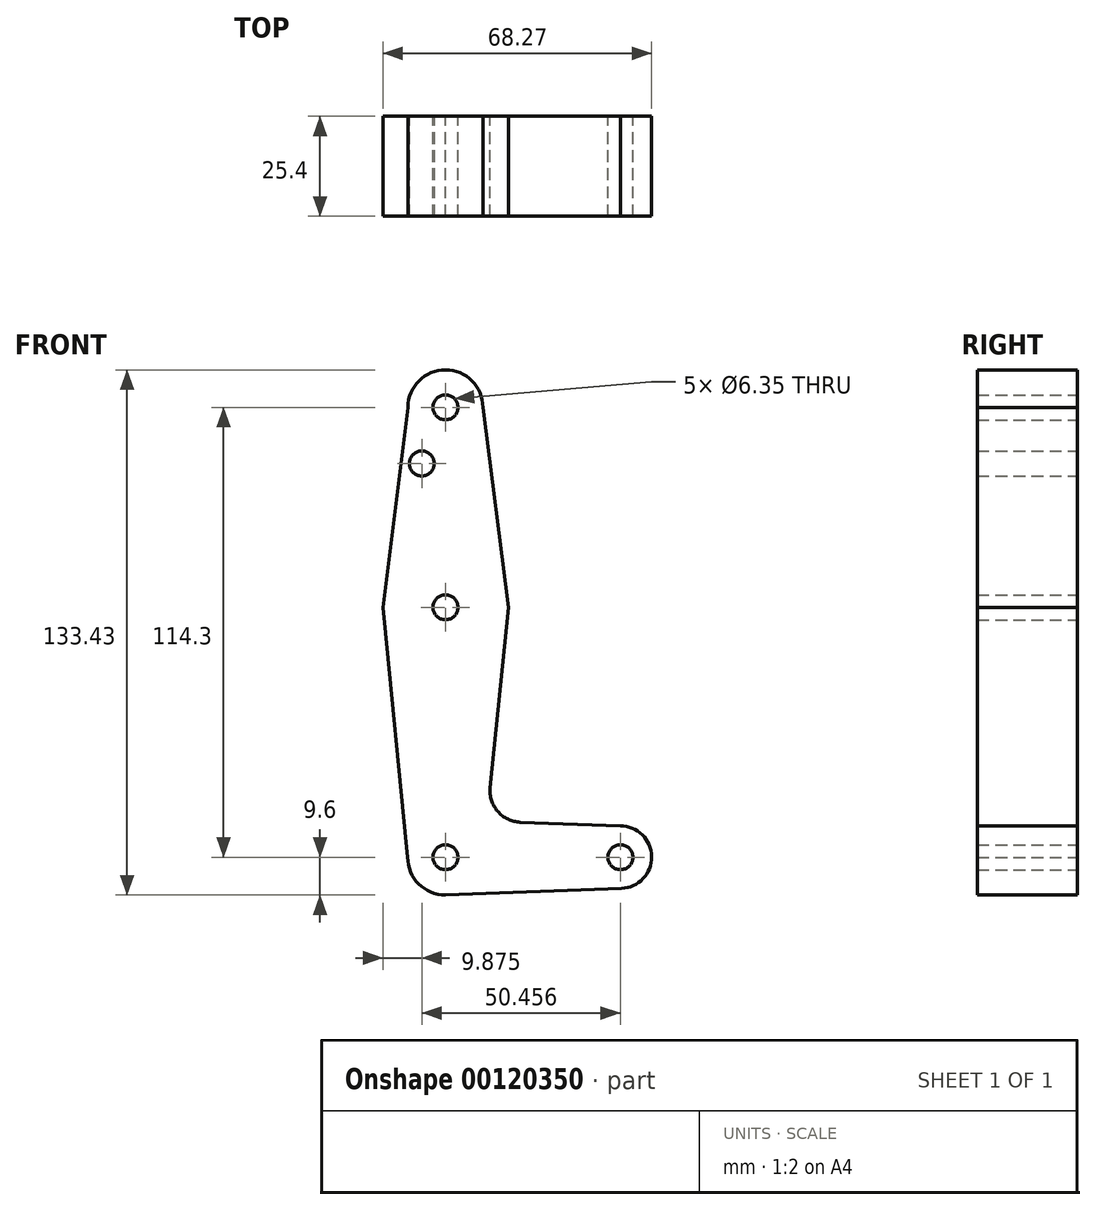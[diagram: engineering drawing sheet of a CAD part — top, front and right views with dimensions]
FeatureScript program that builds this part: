
annotation { "Feature Type Name" : "Feature", "Feature Type Description" : "" }
export const myFeature = defineFeature(function(context is Context, id is Id, definition is map)
    precondition{}
    {
        {
            var Q0;
            Q0=qCreatedBy(makeId("Front.planeOp"),FACE);
            var sketch = newSketch(context, id + "F0", { "sketchPlane" : qUnion([Q0])});
            skLineSegment(sketch, "E0", {"start": v(0, 0) * mm, "end": v(0, 114.3) * mm, "construction": true});
            skLineSegment(sketch, "E1", {"start": v(0, 0) * mm, "end": v(44.45, 0) * mm, "construction": true});
            skCircle(sketch, "E2", {"center": v(0, 0) * mm, "radius": 9.6 * mm});
            skCircle(sketch, "E3", {"center": v(0, 63.5) * mm, "radius": 15.88 * mm});
            skCircle(sketch, "E4", {"center": v(0, 114.3) * mm, "radius": 9.53 * mm});
            skCircle(sketch, "E5", {"center": v(44.45, 0) * mm, "radius": 7.94 * mm});
            skLineSegment(sketch, "E6", {"start": v(-9.52, 114.3) * mm, "end": v(-15.88, 63.5) * mm});
            skLineSegment(sketch, "E7", {"start": v(9.52, 114.3) * mm, "end": v(16, 63.5) * mm});
            skLineSegment(sketch, "E8", {"start": v(44.45, 7.94) * mm, "end": v(19, 8.9) * mm});
            skLineSegment(sketch, "E9", {"start": v(0, -9.6) * mm, "end": v(44.75, -7.93) * mm});
            skLineSegment(sketch, "E10", {"start": v(-9.6, 0) * mm, "end": v(-15.88, 63.5) * mm});
            skLineSegment(sketch, "E11", {"start": v(11.38, 17.64) * mm, "end": v(16, 63.5) * mm});
            skCircle(sketch, "E12", {"center": v(0, 114.3) * mm, "radius": 3.18 * mm});
            skCircle(sketch, "E13", {"center": v(0, 63.5) * mm, "radius": 3.17 * mm});
            skCircle(sketch, "E14", {"center": v(0, 0) * mm, "radius": 3.18 * mm});
            skCircle(sketch, "E15", {"center": v(44.45, 0) * mm, "radius": 3.18 * mm});
            skCircle(sketch, "E16", {"center": v(-6, 100.03) * mm, "radius": 3.18 * mm});
            skArc(sketch, "E17.filletArc", {"start": v(11.38, 17.64) * mm, "mid": v(13.3, 11.62) * mm, "end": v(19, 8.9) * mm});
            skSolve(sketch);
        }
        {
            var Q0;
            {var subQ8=sQuery(id+"F0.wireOp",EDGE,"E8");Q0=makeQuery(id+"F0.imprint","IMPRINT",FACE,{"disambiguationData":[TD([[makeQuery(id+"F0.imprint","IMPRINT",EDGE,{"derivedFrom":subQ8}),1.0]])]});}
            var Q1;
            Q1=makeQuery(id+"F0.imprint","IMPRINT",FACE,{"disambiguationData":[TD([[makeQuery(id+"F0.imprint","IMPRINT",EDGE,{"derivedFrom":sQuery(id+"F0.wireOp",EDGE,"E16")}),-1.0]])]});
            var Q2;
            Q2=makeQuery(id+"F0.imprint","IMPRINT",FACE,{"disambiguationData":[TD([[makeQuery(id+"F0.imprint","IMPRINT",EDGE,{"derivedFrom":sQuery(id+"F0.wireOp",EDGE,"E13")}),-1.0]])]});
            var Q3;
            Q3=makeQuery(id+"F0.imprint","IMPRINT",FACE,{"disambiguationData":[TD([[makeQuery(id+"F0.imprint","IMPRINT",EDGE,{"derivedFrom":sQuery(id+"F0.wireOp",EDGE,"E14")}),-1.0]])]});
            var Q4;
            Q4=makeQuery(id+"F0.imprint","IMPRINT",FACE,{"disambiguationData":[TD([[makeQuery(id+"F0.imprint","IMPRINT",EDGE,{"derivedFrom":sQuery(id+"F0.wireOp",EDGE,"E15")}),-1.0]])]});
            var Q5;
            Q5=makeQuery(id+"F0.imprint","IMPRINT",FACE,{"disambiguationData":[TD([[makeQuery(id+"F0.imprint","IMPRINT",EDGE,{"derivedFrom":sQuery(id+"F0.wireOp",EDGE,"E12")}),-1.0]])]});
            extrude(context, id + "F1", {"entities" : qUnion([Q0, Q1, Q2, Q3, Q4, Q5]), "depth" : 25.4 * mm});
        }
    });
